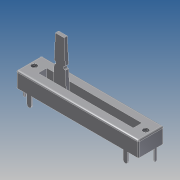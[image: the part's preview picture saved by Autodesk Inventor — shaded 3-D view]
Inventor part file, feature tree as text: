
AUTODESK INVENTOR PART (.ipt)
format: ipt  version: 2012 (Build 160160000, 160)  size: 228,352 bytes
history: native  units: mm
features: extrude x8, sketch x8, fillet x5, thread x2
ambient origin geometry x8: Origin, YZ Plane, XZ Plane, XY Plane, X Axis, Y Axis, Z Axis, Center Point
bodies: Solid1 (feature_tree)
feature tree (23):
  extrude  "Extrusion1"  Depth=9.4mm
  extrude  "Extrusion2"  Depth=3.1mm
  fillet  "Fillet1"  Radius=3.1mm
  fillet  "Fillet2"  Radius=4.3mm
  extrude  "Extrusion3"  Depth=0.5mm
  thread  "Thread1"  [1 undecoded]
  thread  "Thread2"  [1 undecoded]
  extrude  "Extrusion4"  Depth=10.0mm TaperAngle=0.0deg
  fillet  "Fillet3"  Radius=10.0mm
  extrude  "Extrusion5"  Depth=1.6mm
  fillet  "Fillet4"  Radius=4.0mm
  extrude  "Extrusion6"  Depth=1.6mm
  fillet  "Fillet5"  Radius=4.0mm
  extrude  "Extrusion7"  Depth=0.8mm
  extrude  "Extrusion8"  Depth=4.0mm
  sketch  "Sketch1"  dims[d0=45.0mm d1=9.4mm]
  sketch  "Sketch2"  dims[d2=5.6mm d3=0.0mm d6=3.1mm d7=3.1mm d8=4.3mm d9=0.0mm]
  sketch  "Sketch3"  dims[d10=0.5mm d11=0.5mm d12=2.0mm d13=2.0mm]
  sketch  "Sketch4"  dims[d16=4.0mm d17=0.0mm d18=10.0mm d19=0.0mm d20=10.0mm d21=0.0mm]
  sketch  "Sketch5"  dims[d22=4.0mm d23=1.6mm d24=4.0mm]
  sketch  "Sketch6"  dims[d25=4.0mm d26=1.6mm d27=4.0mm]
  sketch  "Sketch8"  dims[d28=0.5mm d29=0.0mm d30=0.8mm]
  sketch  "Sketch9"  dims[d31=1.6mm d32=4.0mm d33=4.0mm d34=1.6mm d35=5.0mm d36=5.0mm d37=0.5mm d38=0.0mm d39=0.8mm d40=0.8mm d41=0.4mm d42=0.4mm d43=0.8mm d44=0.8mm d45=0.4mm d46=2.5mm d47=1.25mm d48=4.3mm d49=0.0mm d50=0.4mm d51=5.0mm d52=3.2mm d53=15.0mm d54=1.2mm d55=0.0mm d56=1.3mm d57=1.3mm d58=9.5mm d59=9.5mm d60=1.2mm d61=0.0mm d62=35.0mm d63=35.0mm d64=17.5mm d65=41.0mm d66=20.5mm]
note: 2 required parameter values undecoded (feature->parameter linkage not recoverable at this tier; creation-order binding heuristic only, values carry confidence <= 0.55)
